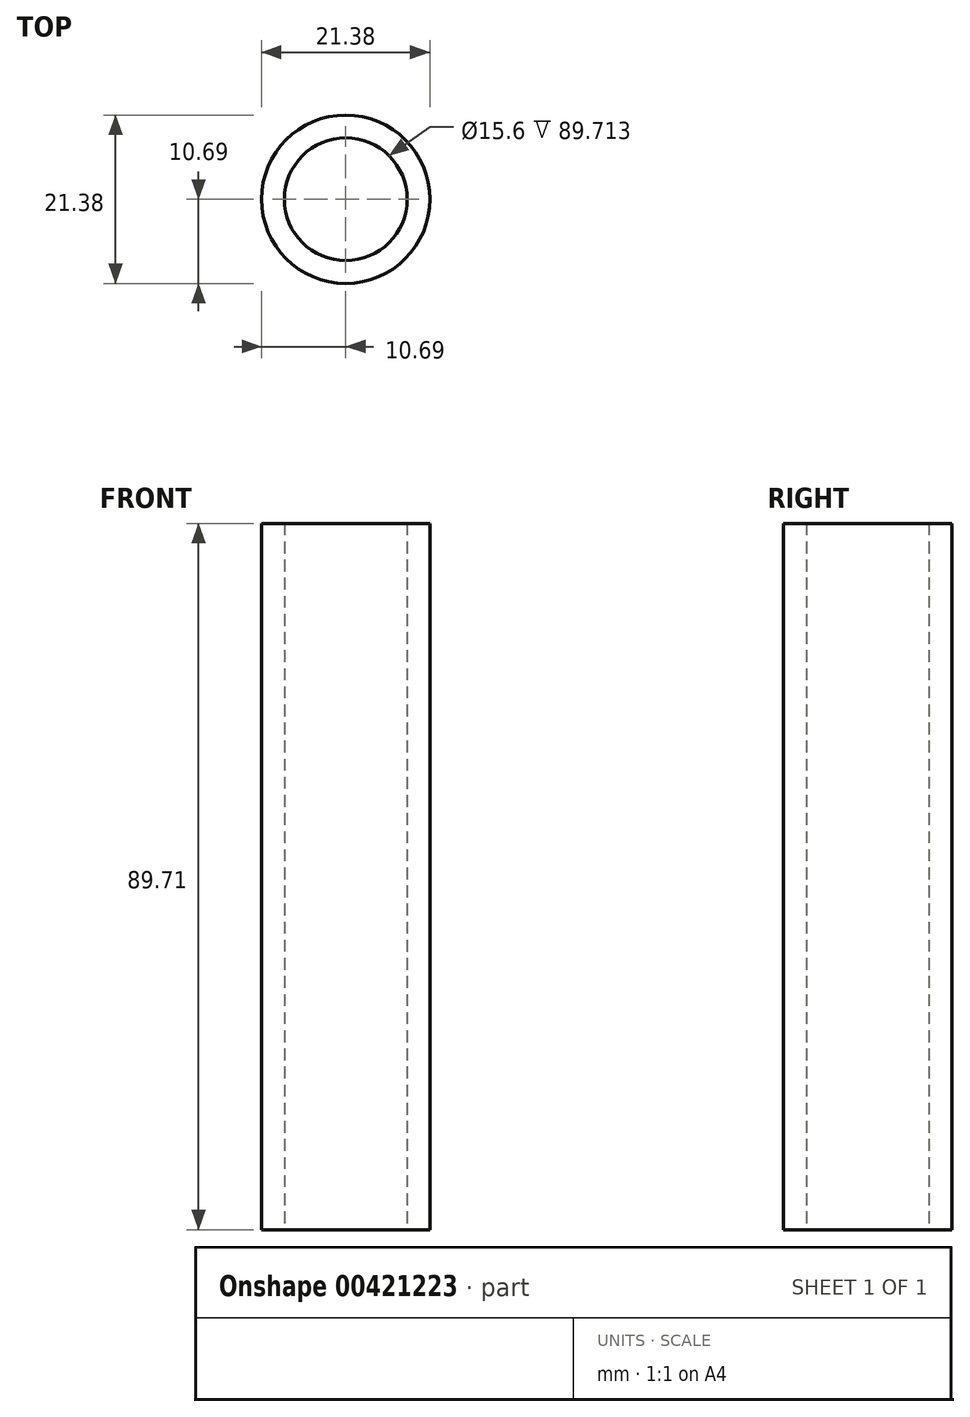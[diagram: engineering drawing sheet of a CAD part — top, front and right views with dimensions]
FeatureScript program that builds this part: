
annotation { "Feature Type Name" : "Feature", "Feature Type Description" : "" }
export const myFeature = defineFeature(function(context is Context, id is Id, definition is map)
    precondition{}
    {
        {
            var Q0;
            Q0=qCreatedBy(makeId("Top.planeOp"),FACE);
            var sketch = newSketch(context, id + "F0", { "sketchPlane" : qUnion([Q0])});
            skCircle(sketch, "E0", {"center": v(0, 0) * mm, "radius": 10.7 * mm});
            skCircle(sketch, "E1", {"center": v(0, 0) * mm, "radius": 7.8 * mm});
            skSolve(sketch);
        }
        {
            var Q0;
            Q0 = qSketchRegion(id + "F0", true);
            extrude(context, id + "F1", {"entities" : qUnion([Q0]), "depth" : 89.7 * mm});
        }
    });
